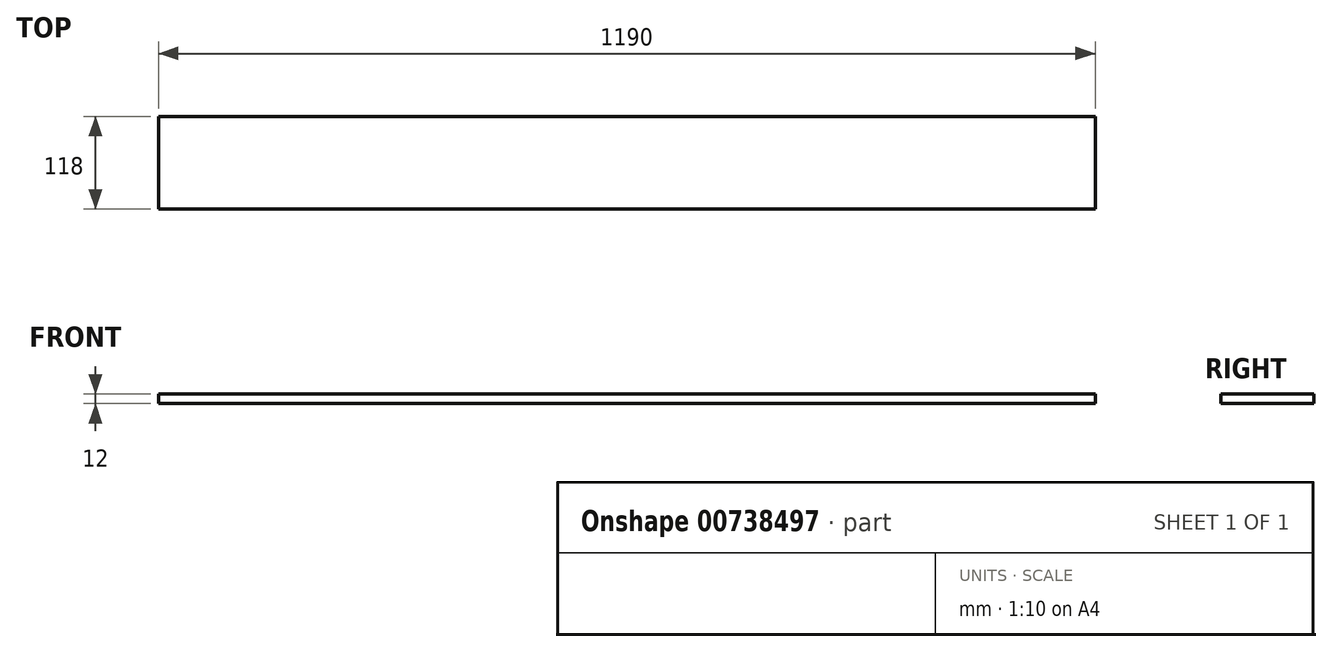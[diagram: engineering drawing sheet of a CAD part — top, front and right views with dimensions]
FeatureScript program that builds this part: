
annotation { "Feature Type Name" : "Feature", "Feature Type Description" : "" }
export const myFeature = defineFeature(function(context is Context, id is Id, definition is map)
    precondition{}
    {
        {
            var Q0;
            Q0=qCreatedBy(makeId("Top.planeOp"),FACE);
            var sketch = newSketch(context, id + "F0", { "sketchPlane" : qUnion([Q0])});
            skLineSegment(sketch, "E0.bottom", {"start": v(0, 0) * mm, "end": v(1190, 0) * mm});
            skLineSegment(sketch, "E0.top", {"start": v(0, 118) * mm, "end": v(1190, 118) * mm});
            skLineSegment(sketch, "E0.left", {"start": v(0, 0) * mm, "end": v(0, 118) * mm});
            skLineSegment(sketch, "E0.right", {"start": v(1190, 0) * mm, "end": v(1190, 118) * mm});
            skSolve(sketch);
        }
        {
            var Q0;
            Q0=makeQuery(id+"F0.imprint","IMPRINT",FACE,{"disambiguationData":[TD([[makeQuery(id+"F0.imprint","IMPRINT",EDGE,{"derivedFrom":sQuery(id+"F0.wireOp",EDGE,"E0.bottom")}),1.0]])]});
            extrude(context, id + "F1", {"entities" : qUnion([Q0]), "depth" : 12 * mm, "offsetDistance" : 25 * mm});
        }
    });
